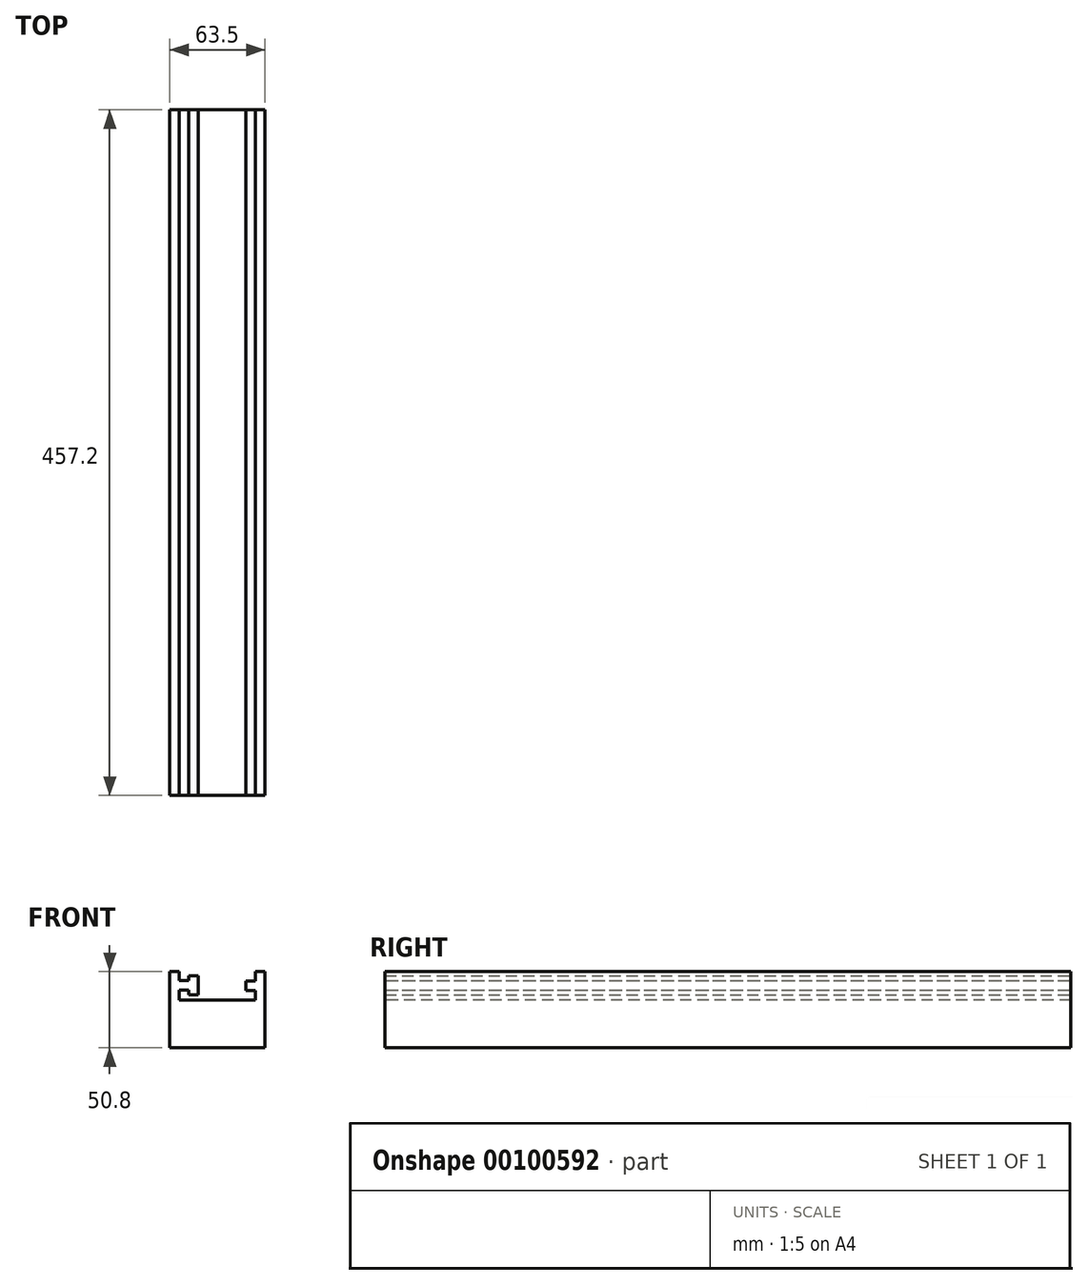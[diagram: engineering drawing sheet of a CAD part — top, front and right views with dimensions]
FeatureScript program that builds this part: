
annotation { "Feature Type Name" : "Feature", "Feature Type Description" : "" }
export const myFeature = defineFeature(function(context is Context, id is Id, definition is map)
    precondition{}
    {
        {
            var Q0;
            Q0=qCreatedBy(makeId("Top.planeOp"),FACE);
            var sketch = newSketch(context, id + "F0", { "sketchPlane" : qUnion([Q0])});
            skLineSegment(sketch, "E0.bottom", {"start": v(-18.01, -38.24) * mm, "end": v(45.49, -38.24) * mm});
            skLineSegment(sketch, "E0.top", {"start": v(-18.01, 418.96) * mm, "end": v(45.49, 418.96) * mm});
            skLineSegment(sketch, "E0.left", {"start": v(-18.01, -38.24) * mm, "end": v(-18.01, 418.96) * mm});
            skLineSegment(sketch, "E0.right", {"start": v(45.49, -38.24) * mm, "end": v(45.49, 418.96) * mm});
            skSolve(sketch);
        }
        {
            var Q0;
            Q0=makeQuery(id+"F0.imprint","IMPRINT",FACE,{"disambiguationData":[TD([[makeQuery(id+"F0.imprint","IMPRINT",EDGE,{"derivedFrom":sQuery(id+"F0.wireOp",EDGE,"E0.bottom")}),1.0]])]});
            extrude(context, id + "F1", {"entities" : qUnion([Q0]), "depth" : 50.8 * mm});
        }
        {
            var Q0;
            Q0=makeQuery(id+"F1.opExtrude","SWEPT_FACE",FACE,{"disambiguationData":[OSD([sQuery(id+"F0.wireOp",EDGE,"E0.bottom")])]});
            var sketch = newSketch(context, id + "F2", { "sketchPlane" : qUnion([Q0])});
            skLineSegment(sketch, "E1.bottom", {"start": v(-11.66, 50.8) * mm, "end": v(39.14, 50.8) * mm});
            skLineSegment(sketch, "E1.top", {"start": v(-11.66, 31.75) * mm, "end": v(39.14, 31.75) * mm});
            skLineSegment(sketch, "E1.left", {"start": v(-11.66, 50.8) * mm, "end": v(-11.66, 31.75) * mm});
            skLineSegment(sketch, "E1.right", {"start": v(39.14, 50.8) * mm, "end": v(39.14, 31.75) * mm});
            skSolve(sketch);
        }
        {
            var Q0;
            Q0=makeQuery(id+"F2.imprint","IMPRINT",FACE,{"disambiguationData":[TD([[makeQuery(id+"F2.imprint","IMPRINT",EDGE,{"derivedFrom":sQuery(id+"F2.wireOp",EDGE,"E1.bottom")}),-1.0]])]});
            extrude(context, id + "F3", {"entities" : qUnion([Q0]), "operationType" : NewBodyOperationType.REMOVE, "oppositeDirection" : true, "depth" : 457.2 * mm});
        }
        {
            var Q0;
            Q0=makeQuery(id+"F3.boolean.opBoolean","COPY",FACE,{"derivedFrom":makeQuery(id+"F3.opExtrude","SWEPT_FACE",FACE,{"disambiguationData":[OSD([sQuery(id+"F2.wireOp",EDGE,"E1.left")])]})});
            var sketch = newSketch(context, id + "F4", { "sketchPlane" : qUnion([Q0])});
            skLineSegment(sketch, "E2.bottom", {"start": v(-38.24, 44.96) * mm, "end": v(418.96, 44.96) * mm});
            skLineSegment(sketch, "E2.top", {"start": v(-38.24, 38.61) * mm, "end": v(418.96, 38.61) * mm});
            skLineSegment(sketch, "E2.left", {"start": v(-38.24, 44.96) * mm, "end": v(-38.24, 38.61) * mm});
            skLineSegment(sketch, "E2.right", {"start": v(418.96, 44.96) * mm, "end": v(418.96, 38.61) * mm});
            skSolve(sketch);
        }
        {
            var Q0;
            Q0=makeQuery(id+"F4.imprint","IMPRINT",FACE,{"disambiguationData":[TD([[makeQuery(id+"F4.imprint","IMPRINT",EDGE,{"derivedFrom":sQuery(id+"F4.wireOp",EDGE,"E2.bottom")}),-1.0]])]});
            extrude(context, id + "F5", {"entities" : qUnion([Q0]), "operationType" : NewBodyOperationType.ADD, "depth" : 6.35 * mm});
        }
        {
            var Q0;
            Q0=makeQuery(id+"F5.opExtrude","CAP_FACE",FACE,{"disambiguationData":[OSD([sQuery(id+"F4.wireOp",EDGE,"E2.bottom"),sQuery(id+"F4.wireOp",EDGE,"E2.top"),sQuery(id+"F4.wireOp",EDGE,"E2.left"),sQuery(id+"F4.wireOp",EDGE,"E2.right")])],"isStart":false});
            var sketch = newSketch(context, id + "F6", { "sketchPlane" : qUnion([Q0])});
            skLineSegment(sketch, "E3.bottom", {"start": v(-38.24, 48.14) * mm, "end": v(418.96, 48.14) * mm});
            skLineSegment(sketch, "E3.top", {"start": v(-38.24, 35.44) * mm, "end": v(418.96, 35.44) * mm});
            skLineSegment(sketch, "E3.left", {"start": v(-38.24, 48.14) * mm, "end": v(-38.24, 35.44) * mm});
            skLineSegment(sketch, "E3.right", {"start": v(418.96, 48.14) * mm, "end": v(418.96, 35.44) * mm});
            skSolve(sketch);
        }
        {
            var Q0;
            {var subQ0=sQuery(id+"F6.wireOp",EDGE,"E3.bottom");Q0=makeQuery(id+"F6.imprint","IMPRINT",FACE,{"disambiguationData":[TD([[makeQuery(id+"F6.imprint","IMPRINT",EDGE,{"derivedFrom":subQ0}),-1.0]])]});}
            var Q1;
            {var subQ1=makeQuery(id+"F5.opExtrude","CAP_EDGE",EDGE,{"disambiguationData":[OSD([sQuery(id+"F4.wireOp",EDGE,"E2.bottom")])],"isStart":false});Q1=makeQuery(id+"F6.imprint","IMPRINT",FACE,{"disambiguationData":[TD([[makeQuery(id+"F6.imprint","IMPRINT",EDGE,{"derivedFrom":subQ1}),-1.0]])]});}
            var Q2;
            {var subQ0=sQuery(id+"F6.wireOp",EDGE,"E3.top");Q2=makeQuery(id+"F6.imprint","IMPRINT",FACE,{"disambiguationData":[TD([[makeQuery(id+"F6.imprint","IMPRINT",EDGE,{"derivedFrom":subQ0}),1.0]])]});}
            extrude(context, id + "F7", {"entities" : qUnion([Q0, Q1, Q2]), "operationType" : NewBodyOperationType.ADD, "depth" : 6.35 * mm});
        }
        {
            var Q0;
            Q0=makeQuery(id+"F3.boolean.opBoolean","COPY",FACE,{"derivedFrom":makeQuery(id+"F3.opExtrude","SWEPT_FACE",FACE,{"disambiguationData":[OSD([sQuery(id+"F2.wireOp",EDGE,"E1.right")])]})});
            var sketch = newSketch(context, id + "F8", { "sketchPlane" : qUnion([Q0])});
            skLineSegment(sketch, "E4.bottom", {"start": v(-418.96, 44.45) * mm, "end": v(38.24, 44.45) * mm});
            skLineSegment(sketch, "E4.top", {"start": v(-418.96, 38.1) * mm, "end": v(38.24, 38.1) * mm});
            skLineSegment(sketch, "E4.left", {"start": v(-418.96, 44.45) * mm, "end": v(-418.96, 38.1) * mm});
            skLineSegment(sketch, "E4.right", {"start": v(38.24, 44.45) * mm, "end": v(38.24, 38.1) * mm});
            skSolve(sketch);
        }
        {
            var Q0;
            Q0=makeQuery(id+"F8.imprint","IMPRINT",FACE,{"disambiguationData":[TD([[makeQuery(id+"F8.imprint","IMPRINT",EDGE,{"derivedFrom":sQuery(id+"F8.wireOp",EDGE,"E4.bottom")}),-1.0]])]});
            extrude(context, id + "F9", {"entities" : qUnion([Q0]), "operationType" : NewBodyOperationType.ADD, "depth" : 6.35 * mm});
        }
    });
